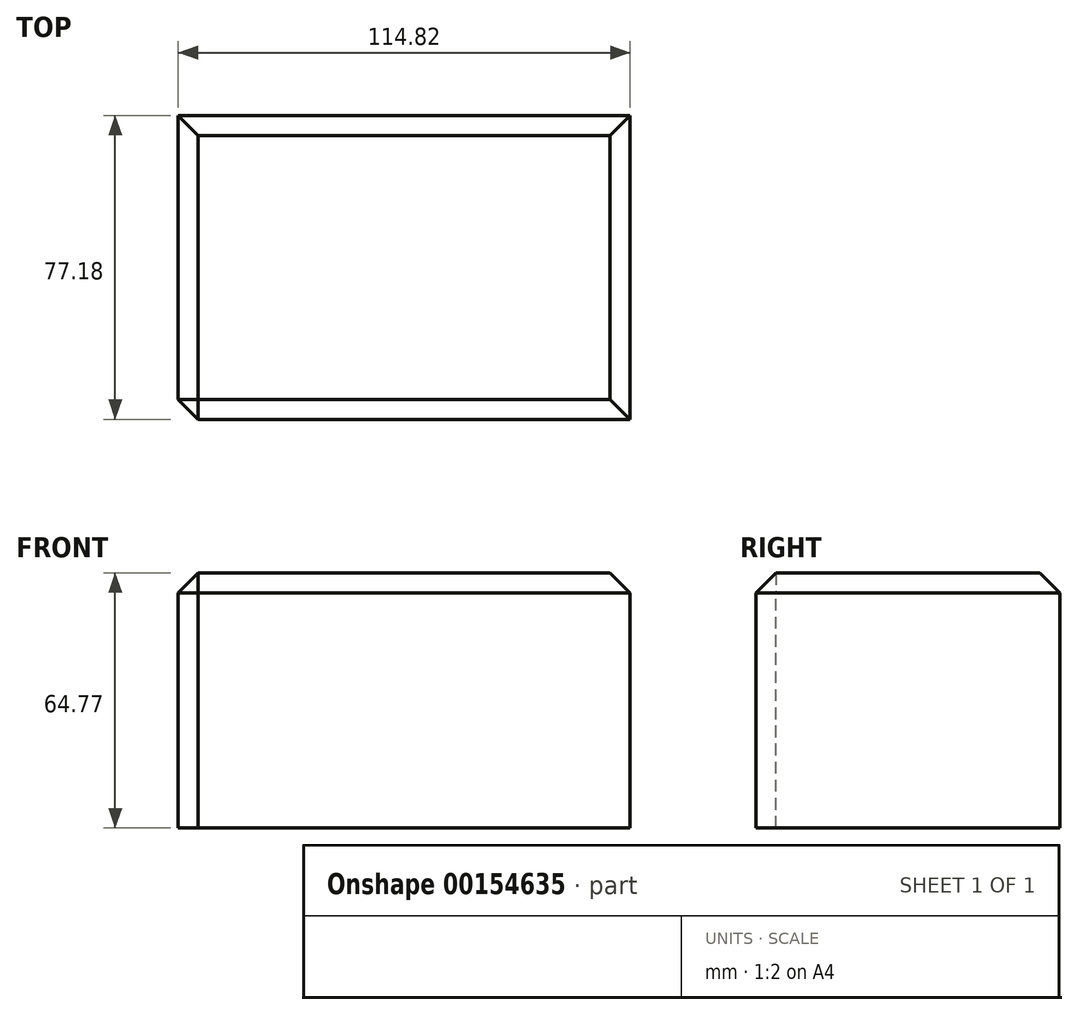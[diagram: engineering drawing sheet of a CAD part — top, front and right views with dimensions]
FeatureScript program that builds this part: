
annotation { "Feature Type Name" : "Feature", "Feature Type Description" : "" }
export const myFeature = defineFeature(function(context is Context, id is Id, definition is map)
    precondition{}
    {
        {
            var Q0;
            Q0=qCreatedBy(makeId("Top.planeOp"),FACE);
            var sketch = newSketch(context, id + "F0", { "sketchPlane" : qUnion([Q0])});
            skLineSegment(sketch, "E0.bottom", {"start": v(0, 0) * mm, "end": v(-114.82, 0) * mm});
            skLineSegment(sketch, "E0.top", {"start": v(0, -77.18) * mm, "end": v(-114.82, -77.18) * mm});
            skLineSegment(sketch, "E0.left", {"start": v(0, 0) * mm, "end": v(0, -77.18) * mm});
            skLineSegment(sketch, "E0.right", {"start": v(-114.82, 0) * mm, "end": v(-114.82, -77.18) * mm});
            skSolve(sketch);
        }
        {
            var Q0;
            Q0=makeQuery(id+"F0.imprint","IMPRINT",FACE,{"disambiguationData":[TD([[makeQuery(id+"F0.imprint","IMPRINT",EDGE,{"derivedFrom":sQuery(id+"F0.wireOp",EDGE,"E0.bottom")}),1.0]])]});
            extrude(context, id + "F1", {"entities" : qUnion([Q0]), "depth" : 64.77 * mm});
        }
        {
            var Q0;
            Q0=makeQuery(id+"F1.opExtrude","CAP_EDGE",EDGE,{"disambiguationData":[OSD([sQuery(id+"F0.wireOp",EDGE,"E0.right")])],"isStart":false});
            var Q1;
            Q1=makeQuery(id+"F1.opExtrude","CAP_EDGE",EDGE,{"disambiguationData":[OSD([sQuery(id+"F0.wireOp",EDGE,"E0.bottom")])],"isStart":false});
            var Q2;
            Q2=makeQuery(id+"F1.opExtrude","CAP_EDGE",EDGE,{"disambiguationData":[OSD([sQuery(id+"F0.wireOp",EDGE,"E0.left")])],"isStart":false});
            var Q3;
            Q3=makeQuery(id+"F1.opExtrude","CAP_EDGE",EDGE,{"disambiguationData":[OSD([sQuery(id+"F0.wireOp",EDGE,"E0.top")])],"isStart":false});
            var Q4;
            Q4=makeQuery(id+"F1.opExtrude","SWEPT_EDGE",EDGE,{"disambiguationData":[OSD([sQuery(id+"F0.wireOp",EDGE,"E0.top"),sQuery(id+"F0.wireOp",EDGE,"E0.right")])]});
            chamfer(context, id + "F2", {"entities" : qUnion([Q0, Q1, Q2, Q3, Q4]), "width" : 5.08 * mm, "tangentPropagation" : true});
        }
    });
